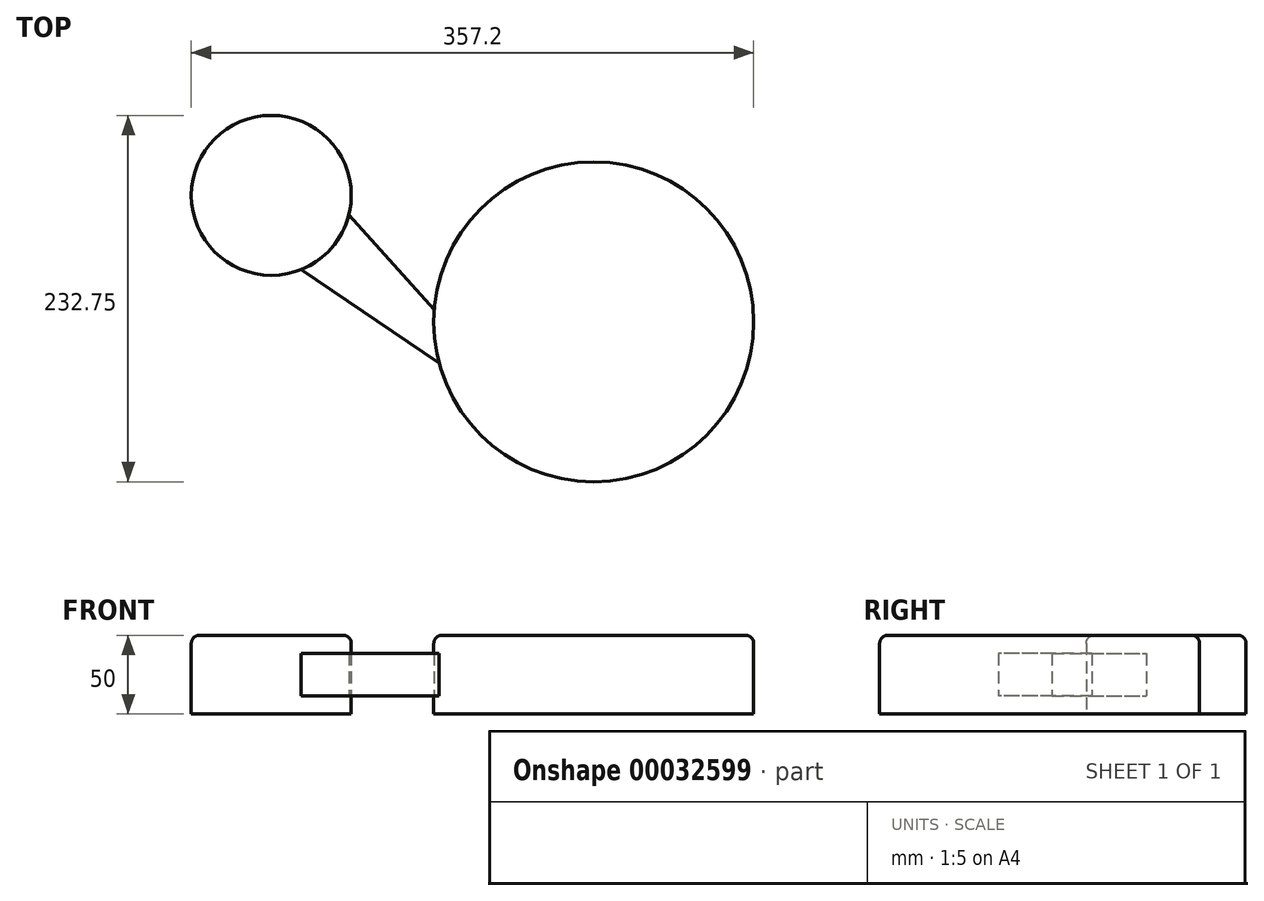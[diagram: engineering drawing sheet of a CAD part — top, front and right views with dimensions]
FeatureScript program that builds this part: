
annotation { "Feature Type Name" : "Feature", "Feature Type Description" : "" }
export const myFeature = defineFeature(function(context is Context, id is Id, definition is map)
    precondition{}
    {
        {
            var Q0;
            Q0=qCreatedBy(makeId("Top.planeOp"),FACE);
            var sketch = newSketch(context, id + "F0", { "sketchPlane" : qUnion([Q0])});
            skLineSegment(sketch, "E0", {"start": v(0, 0) * mm, "end": v(204.8, 0) * mm, "construction": true});
            skLineSegment(sketch, "E1", {"start": v(0, 0) * mm, "end": v(0, 80.35) * mm, "construction": true});
            skCircle(sketch, "E2", {"center": v(204.8, 0) * mm, "radius": 101.6 * mm});
            skCircle(sketch, "E3", {"center": v(0, 80.35) * mm, "radius": 50.8 * mm});
            skSolve(sketch);
        }
        {
            var Q0;
            Q0=makeQuery(id+"F0.imprint","IMPRINT",FACE,{"disambiguationData":[TD([[makeQuery(id+"F0.imprint","IMPRINT",EDGE,{"derivedFrom":sQuery(id+"F0.wireOp",EDGE,"E2")}),1.0]])]});
            var Q1;
            Q1=makeQuery(id+"F0.imprint","IMPRINT",FACE,{"disambiguationData":[TD([[makeQuery(id+"F0.imprint","IMPRINT",EDGE,{"derivedFrom":sQuery(id+"F0.wireOp",EDGE,"E3")}),1.0]])]});
            extrude(context, id + "F1", {"entities" : qUnion([Q0, Q1]), "endBound" : BoundingType.SYMMETRIC, "depth" : 50 * mm});
        }
        {
            var Q0;
            Q0=makeQuery(id+"F1.opExtrude","CAP_EDGE",EDGE,{"disambiguationData":[OSD([sQuery(id+"F0.wireOp",EDGE,"E3")])],"isStart":false});
            var Q1;
            Q1=makeQuery(id+"F1.opExtrude","CAP_EDGE",EDGE,{"disambiguationData":[OSD([sQuery(id+"F0.wireOp",EDGE,"E2")])],"isStart":false});
            fillet(context, id + "F2", {"entities" : qUnion([Q0, Q1]), "radius" : 5.08 * mm, "tangentPropagation" : true, "allowEdgeOverflow" : false});
        }
        {
            var Q0;
            Q0=qCreatedBy(makeId("Top.planeOp"),FACE);
            var sketch = newSketch(context, id + "F3", { "sketchPlane" : qUnion([Q0])});
            skLineSegment(sketch, "E4", {"start": v(17.45, 34.35) * mm, "end": v(178.08, -74.55) * mm});
            skLineSegment(sketch, "E5", {"start": v(178.08, -74.55) * mm, "end": v(10.49, 110.72) * mm});
            skLineSegment(sketch, "E6", {"start": v(10.49, 110.72) * mm, "end": v(17.45, 34.35) * mm});
            skSolve(sketch);
        }
        {
            var Q0;
            Q0=makeQuery(id+"F3.imprint","IMPRINT",FACE,{"disambiguationData":[TD([[makeQuery(id+"F3.imprint","IMPRINT",EDGE,{"derivedFrom":sQuery(id+"F3.wireOp",EDGE,"E4")}),1.0]])]});
            extrude(context, id + "F4", {"entities" : qUnion([Q0]), "operationType" : NewBodyOperationType.ADD, "endBound" : BoundingType.SYMMETRIC, "depth" : 27 * mm});
        }
    });
